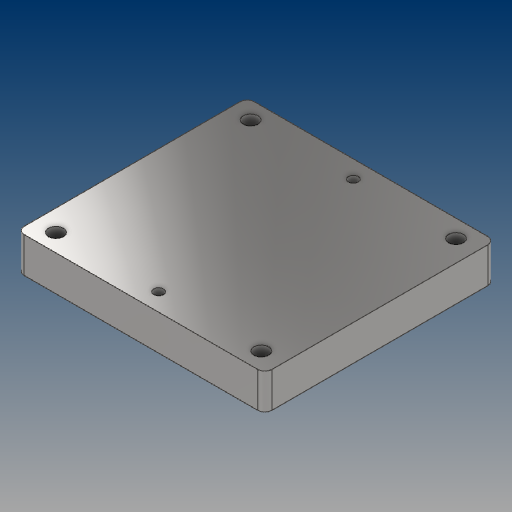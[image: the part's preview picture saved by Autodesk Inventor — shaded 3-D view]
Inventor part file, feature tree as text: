
AUTODESK INVENTOR PART (.ipt)
format: ipt  version: 2021 (Build 250183000, 183)  size: 177,664 bytes
history: native  units: mm
features: sketch x3, hole x2, mirror x2, projected_geometry x2, extrude x1, fillet x1
ambient origin geometry x8: Origin, YZ Plane, XZ Plane, XY Plane, X Axis, Y Axis, Z Axis, Center Point
bodies: Solid1 (feature_tree)
feature tree (11):
  extrude  "Extrusion1"  Depth=65.0mm
  hole  "Hole1"  [1 undecoded]
  mirror  "Mirror1"
  mirror  "Mirror2"
  fillet  "Fillet1"  Radius=10.0mm
  hole  "Hole2"  [1 undecoded]
  sketch  "Sketch1"  dims[d0=70.0mm d1=65.0mm]
  sketch  "Sketch2"  dims[d2=10.0mm d3=10.0mm d4=0.0mm d5=10.0mm]
  projected_geometry  "Projected Loop1"
  sketch  "Sketch3"  dims[d6=6.0mm d7=4.2mm d8=6.0mm d9=8.0mm d10=4.0mm d11=90.0deg d12=8.0mm d13=20.594885mm d14=2.0mm d15=2.8mm d16=6.0mm d17=8.0mm d18=4.0mm d19=90.0deg d20=8.0mm d21=20.594885mm]
  projected_geometry  "Projected Loop2"
note: 2 required parameter values undecoded (feature->parameter linkage not recoverable at this tier; creation-order binding heuristic only, values carry confidence <= 0.55)
